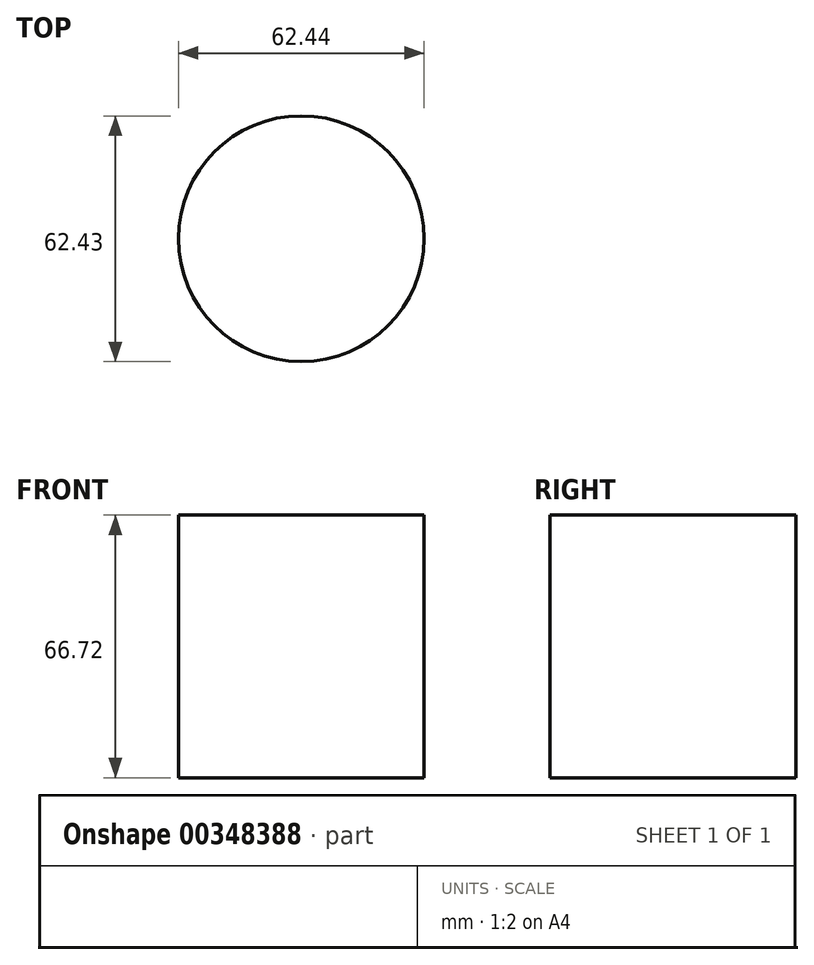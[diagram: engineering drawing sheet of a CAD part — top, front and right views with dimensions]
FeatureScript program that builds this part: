
annotation { "Feature Type Name" : "Feature", "Feature Type Description" : "" }
export const myFeature = defineFeature(function(context is Context, id is Id, definition is map)
    precondition{}
    {
        {
            var Q0;
            Q0=qCreatedBy(makeId("Top.planeOp"),FACE);
            var sketch = newSketch(context, id + "F0", { "sketchPlane" : qUnion([Q0])});
            skCircle(sketch, "E0", {"center": v(16.24, 38.43) * mm, "radius": 31.22 * mm});
            skSolve(sketch);
        }
        {
            var Q0;
            Q0 = qSketchRegion(id + "F0", true);
            extrude(context, id + "F1", {"entities" : qUnion([Q0]), "depth" : 66.72 * mm});
        }
    });
